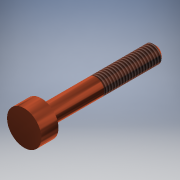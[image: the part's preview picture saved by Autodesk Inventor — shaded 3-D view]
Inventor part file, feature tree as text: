
AUTODESK INVENTOR PART (.ipt)
format: ipt  version: 2017 (Build 210142000, 142)  size: 116,224 bytes
history: native  units: mm
features: extrude x2, sketch x2, thread x1, chamfer x1
ambient origin geometry x8: Origin, YZ Plane, XZ Plane, XY Plane, X Axis, Y Axis, Z Axis, Center Point
bodies: Solid1 (feature_tree)
feature tree (6):
  extrude  "Extrusion1"  Depth=3.0mm TaperAngle=0.0deg
  extrude  "Extrusion2"  Depth=20.0mm TaperAngle=0.0deg
  thread  "Thread1"  [1 undecoded]
  chamfer  "Chamfer1"  Distance=0.5mm Angle=45.0deg
  sketch  "Sketch1"  dims[d0=6.0mm d1=3.0mm d2=0.0mm]
  sketch  "Sketch2"  dims[d3=3.0mm d4=20.0mm d5=0.0mm d6=10.0mm d7=0.5mm d8=0.5mm d9=2.0mm d10=45.0deg]
note: 1 required parameter value undecoded (feature->parameter linkage not recoverable at this tier; creation-order binding heuristic only, values carry confidence <= 0.55)
